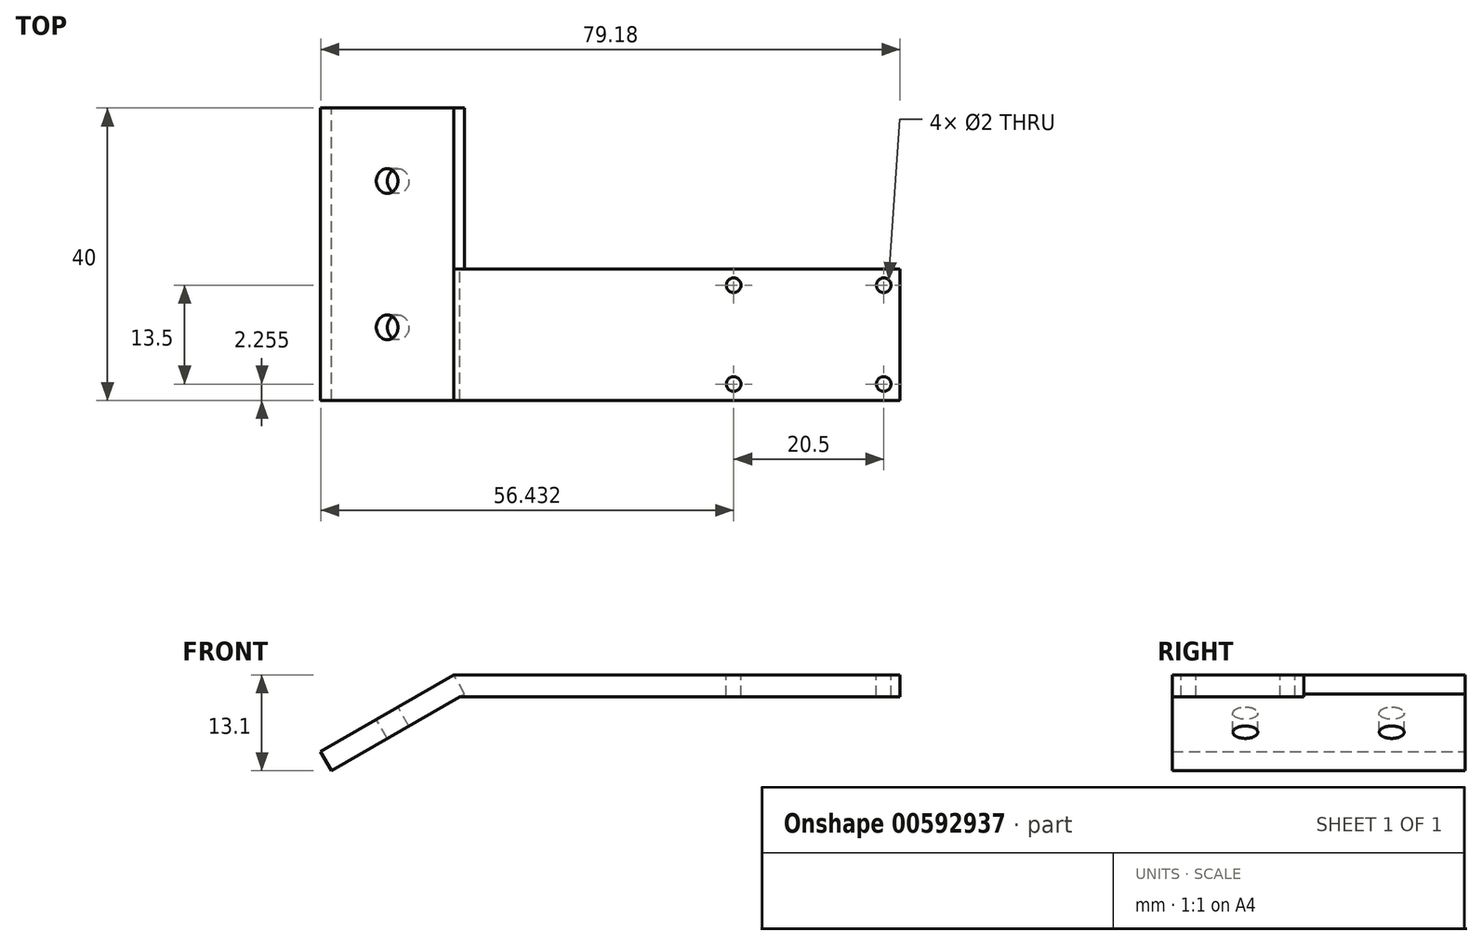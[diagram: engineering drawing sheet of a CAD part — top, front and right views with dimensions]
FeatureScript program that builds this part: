
annotation { "Feature Type Name" : "Feature", "Feature Type Description" : "" }
export const myFeature = defineFeature(function(context is Context, id is Id, definition is map)
    precondition{}
    {
        {
            var Q0;
            Q0=qCreatedBy(makeId("Top.planeOp"),FACE);
            var sketch = newSketch(context, id + "F0", { "sketchPlane" : qUnion([Q0])});
            skLineSegment(sketch, "E0.bottom", {"start": v(-26.58, 10.6) * mm, "end": v(-6.08, 10.6) * mm, "construction": true});
            skLineSegment(sketch, "E0.top", {"start": v(-26.58, -2.9) * mm, "end": v(-6.08, -2.9) * mm, "construction": true});
            skLineSegment(sketch, "E0.left", {"start": v(-26.58, 10.6) * mm, "end": v(-26.58, -2.9) * mm, "construction": true});
            skLineSegment(sketch, "E0.right", {"start": v(-6.08, 10.6) * mm, "end": v(-6.08, -2.9) * mm, "construction": true});
            skLineSegment(sketch, "E1.bottom", {"start": v(-28.83, 12.84) * mm, "end": v(-3.83, 12.84) * mm});
            skLineSegment(sketch, "E1.top", {"start": v(-28.83, -5.16) * mm, "end": v(-3.83, -5.16) * mm});
            skLineSegment(sketch, "E1.left", {"start": v(-28.83, 12.84) * mm, "end": v(-28.83, -5.16) * mm});
            skLineSegment(sketch, "E1.right", {"start": v(-3.83, 12.84) * mm, "end": v(-3.83, -5.16) * mm});
            skPoint(sketch, "E2", {"position": v(-16.33, 10.6) * mm});
            skPoint(sketch, "E3", {"position": v(-16.33, 12.84) * mm});
            skLineSegment(sketch, "E4.bottom", {"start": v(-6.08, 10.6) * mm, "end": v(-3.83, 10.6) * mm, "construction": true});
            skLineSegment(sketch, "E4.top", {"start": v(-6.08, 12.84) * mm, "end": v(-3.83, 12.84) * mm, "construction": true});
            skLineSegment(sketch, "E4.left", {"start": v(-6.08, 10.6) * mm, "end": v(-6.08, 12.84) * mm, "construction": true});
            skLineSegment(sketch, "E4.right", {"start": v(-3.83, 10.6) * mm, "end": v(-3.83, 12.84) * mm, "construction": true});
            skLineSegment(sketch, "E5.bottom", {"start": v(-6.08, -2.9) * mm, "end": v(-3.83, -2.9) * mm, "construction": true});
            skLineSegment(sketch, "E5.top", {"start": v(-6.08, -5.16) * mm, "end": v(-3.83, -5.16) * mm, "construction": true});
            skLineSegment(sketch, "E5.left", {"start": v(-6.08, -2.9) * mm, "end": v(-6.08, -5.16) * mm, "construction": true});
            skLineSegment(sketch, "E5.right", {"start": v(-3.83, -2.9) * mm, "end": v(-3.83, -5.16) * mm, "construction": true});
            skLineSegment(sketch, "E6.bottom", {"start": v(-28.83, 12.84) * mm, "end": v(-64.83, 12.84) * mm});
            skLineSegment(sketch, "E6.top", {"start": v(-28.83, -5.16) * mm, "end": v(-64.83, -5.16) * mm});
            skLineSegment(sketch, "E6.right", {"start": v(-64.83, 12.84) * mm, "end": v(-64.83, -5.16) * mm});
            skSolve(sketch);
        }
        {
            var Q0;
            Q0=makeQuery(id+"F0.imprint","IMPRINT",FACE,{"disambiguationData":[TD([[makeQuery(id+"F0.imprint","IMPRINT",EDGE,{"derivedFrom":sQuery(id+"F0.wireOp",EDGE,"E1.bottom")}),-1.0]])]});
            var Q1;
            Q1=makeQuery(id+"F0.imprint","IMPRINT",FACE,{"disambiguationData":[TD([[makeQuery(id+"F0.imprint","IMPRINT",EDGE,{"derivedFrom":sQuery(id+"F0.wireOp",EDGE,"E1.left")}),-1.0]])]});
            extrude(context, id + "F1", {"entities" : qUnion([Q0, Q1]), "oppositeDirection" : true, "depth" : 3 * mm, "offsetDistance" : 25 * mm});
        }
        {
            var Q0;
            Q0=sQuery(id+"F0.wireOp",VERTEX,"E0.bottom.start");
            var Q1;
            Q1=sQuery(id+"F0.wireOp",VERTEX,"E0.bottom.end");
            var Q2;
            Q2=sQuery(id+"F0.wireOp",VERTEX,"E0.top.end");
            var Q3;
            Q3=sQuery(id+"F0.wireOp",VERTEX,"E0.top.start");
            var Q4;
            Q4=makeQuery(id+"F1.opExtrude","SWEPT_BODY",BODY,{"disambiguationData":[OSD([sQuery(id+"F0.wireOp",EDGE,"E1.bottom"),sQuery(id+"F0.wireOp",EDGE,"E1.top"),sQuery(id+"F0.wireOp",EDGE,"E1.left"),sQuery(id+"F0.wireOp",EDGE,"E1.right")])]});
            hole(context, id + "F2", {"style" : HoleStyle.SIMPLE, "endStyle" : HoleEndStyle.BLIND, "holeDiameter" : 2 * mm, "majorDiameter" : 1.8 * mm, "holeDepth" : 8 * mm, "isTappedThrough" : true, "tappedDepth" : 8 * mm, "tapClearance" : 0, "locations" : qUnion([Q0, Q1, Q2, Q3]), "scope" : qUnion([Q4])});
        }
        {
            var Q0;
            Q0=sQuery(id+"F0.wireOp",EDGE,"E6.right");
            cPlane(context, id + "F3", {"entities" : qUnion([Q0]), "cplaneType" : CPlaneType.LINE_ANGLE, "offset" : 25 * mm, "angle" : 30 * degree, "width" : 150 * mm, "height" : 150 * mm});
        }
        {
            var Q0;
            Q0=qCreatedBy(id+"F3.planeOp",FACE);
            var sketch = newSketch(context, id + "F4", { "sketchPlane" : qUnion([Q0])});
            skLineSegment(sketch, "E7.bottom", {"start": v(-56.14, -12.84) * mm, "end": v(-77.14, -12.84) * mm});
            skLineSegment(sketch, "E7.top", {"start": v(-56.14, 5.16) * mm, "end": v(-77.14, 5.16) * mm});
            skLineSegment(sketch, "E7.left", {"start": v(-56.14, 5.16) * mm, "end": v(-56.14, -12.84) * mm});
            skLineSegment(sketch, "E7.right", {"start": v(-77.14, 5.16) * mm, "end": v(-77.14, -12.84) * mm});
            skLineSegment(sketch, "E8.bottom", {"start": v(-77.14, -12.84) * mm, "end": v(-56.14, -12.84) * mm});
            skLineSegment(sketch, "E8.top", {"start": v(-77.14, -34.84) * mm, "end": v(-56.14, -34.84) * mm});
            skLineSegment(sketch, "E8.left", {"start": v(-77.14, -12.84) * mm, "end": v(-77.14, -34.84) * mm});
            skLineSegment(sketch, "E8.right", {"start": v(-56.14, -12.84) * mm, "end": v(-56.14, -34.84) * mm});
            skLineSegment(sketch, "E9.bottom", {"start": v(-77.14, 5.16) * mm, "end": v(-56.14, 5.16) * mm});
            skPoint(sketch, "E10", {"position": v(-66.64, -34.84) * mm});
            skLineSegment(sketch, "E11", {"start": v(-66.64, -34.84) * mm, "end": v(-66.64, 5.16) * mm, "construction": true});
            skPoint(sketch, "E12", {"position": v(-66.64, -24.84) * mm});
            skPoint(sketch, "E13", {"position": v(-66.64, -4.84) * mm});
            skSolve(sketch);
        }
        {
            var Q0;
            Q0=makeQuery(id+"F4.imprint","IMPRINT",FACE,{"disambiguationData":[TD([[makeQuery(id+"F4.imprint","IMPRINT",EDGE,{"derivedFrom":sQuery(id+"F4.wireOp",EDGE,"E7.bottom")}),-1.0]])]});
            var Q1;
            Q1=makeQuery(id+"F4.imprint","IMPRINT",FACE,{"disambiguationData":[TD([[makeQuery(id+"F4.imprint","IMPRINT",EDGE,{"derivedFrom":sQuery(id+"F4.wireOp",EDGE,"E7.bottom")}),1.0]])]});
            var Q2;
            Q2=makeQuery(id+"F4.imprint","IMPRINT",FACE,{"disambiguationData":[TD([[makeQuery(id+"F4.imprint","IMPRINT",EDGE,{"derivedFrom":sQuery(id+"F4.wireOp",EDGE,"E7.top")}),-1.0]])]});
            var Q3;
            Q3=makeQuery(id+"F1.opExtrude","CAP_FACE",FACE,{"disambiguationData":[OSD([sQuery(id+"F0.wireOp",EDGE,"E1.bottom"),sQuery(id+"F0.wireOp",EDGE,"E1.top"),sQuery(id+"F0.wireOp",EDGE,"E1.right"),sQuery(id+"F0.wireOp",EDGE,"E6.bottom"),sQuery(id+"F0.wireOp",EDGE,"E6.top"),sQuery(id+"F0.wireOp",EDGE,"E6.right")])],"isStart":false});
            extrude(context, id + "F5", {"entities" : qUnion([Q0, Q1, Q2]), "operationType" : NewBodyOperationType.ADD, "depth" : 3 * mm, "endBoundEntityFace" : qUnion([Q3]), "offsetDistance" : 25 * mm});
        }
        {
            var Q0;
            Q0=sQuery(id+"F4.wireOp",VERTEX,"E12");
            var Q1;
            Q1=sQuery(id+"F4.wireOp",VERTEX,"E13");
            var Q2;
            Q2=makeQuery(id+"F1.opExtrude","SWEPT_BODY",BODY,{"disambiguationData":[OSD([sQuery(id+"F0.wireOp",EDGE,"E1.bottom"),sQuery(id+"F0.wireOp",EDGE,"E1.top"),sQuery(id+"F0.wireOp",EDGE,"E1.right"),sQuery(id+"F0.wireOp",EDGE,"E6.bottom"),sQuery(id+"F0.wireOp",EDGE,"E6.top"),sQuery(id+"F0.wireOp",EDGE,"E6.right")])]});
            hole(context, id + "F6", {"style" : HoleStyle.SIMPLE, "endStyle" : HoleEndStyle.BLIND, "oppositeDirection" : true, "standardTappedOrClearance" : lookupTablePath({ "fit" : "Normal", "standard" : "ISO", "size" : "M3", "type" : "Clearance" }), "standardBlindInLast" : lookupTablePath({ "fit" : "Normal", "standard" : "ISO", "engagement" : "75%", "pitch" : "0.5 mm", "size" : "M3", "type" : "Clearance & tapped" }), "holeDiameter" : 3.4 * mm, "majorDiameter" : 5 * mm, "holeDepth" : 8 * mm, "isTappedThrough" : true, "tappedDepth" : 8 * mm, "tapClearance" : 0, "locations" : qUnion([Q0, Q1]), "scope" : qUnion([Q2])});
        }
    });
